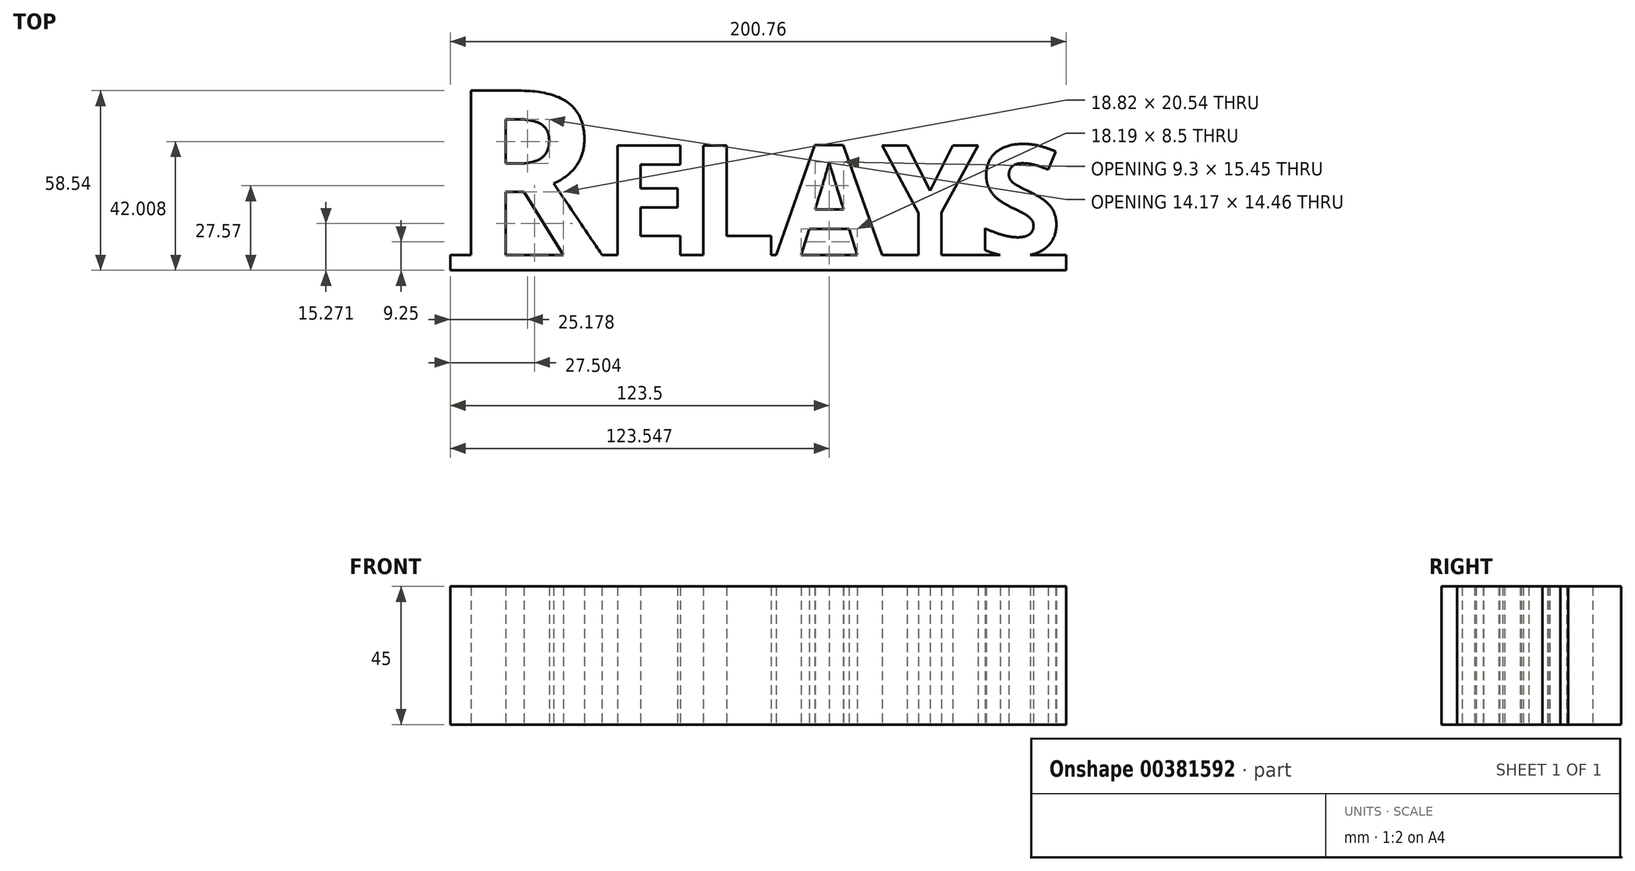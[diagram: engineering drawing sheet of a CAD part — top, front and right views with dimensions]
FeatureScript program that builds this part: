
annotation { "Feature Type Name" : "Feature", "Feature Type Description" : "" }
export const myFeature = defineFeature(function(context is Context, id is Id, definition is map)
    precondition{}
    {
        {
            var Q0;
            Q0=qCreatedBy(makeId("Top.planeOp"),FACE);
            var sketch = newSketch(context, id + "F0", { "sketchPlane" : qUnion([Q0])});
            skText(sketch, "E0", { "text": "ELAYS", "fontName": "OpenSans-Bold.ttf"});
            skText(sketch, "E1", { "text": "R", "fontName": "OpenSans-Bold.ttf"});
            skLineSegment(sketch, "E2", {"start": v(-50, 0) * mm, "end": v(150.76, 0) * mm});
            skLineSegment(sketch, "E3", {"start": v(150.76, -5) * mm, "end": v(-50, -5) * mm});
            skLineSegment(sketch, "E4", {"start": v(-50, -5) * mm, "end": v(-50, 0) * mm});
            skLineSegment(sketch, "E5", {"start": v(150.76, -5) * mm, "end": v(150.76, 0) * mm});
            const initialGuessF0  = {"E0": [0, 0, 1, 0, 0.036], "E1": [-0.05, 0, 1, 0, 0.054]};
            skSetInitialGuess(sketch, initialGuessF0);
            skSolve(sketch);
        }
        {
            var Q0;
            Q0=makeQuery(id+"F0.imprint","IMPRINT",FACE,{"disambiguationData":[TD([[makeQuery(id+"F0.imprint","IMPRINT",EDGE,{"derivedFrom":sQuery(id+"F0.wireOp",EDGE,"E3")}),-1.0]])]});
            extrude(context, id + "F1", {"entities" : qUnion([Q0]), "depth" : 45 * mm, "offsetDistance" : 25 * mm});
        }
        {
            var Q0;
            Q0=makeQuery(id+"F0.imprint","IMPRINT",FACE,{"disambiguationData":[TD([[makeQuery(id+"F0.imprint","IMPRINT",EDGE,{"derivedFrom":sQuery(id+"F0.wireOp",EDGE,"E1.sketch_text.stroke-0")}),-1.0]])]});
            var Q1;
            {var subQ0=sQuery(id+"F0.wireOp",EDGE,"E0.sketch_text.stroke-1");Q1=makeQuery(id+"F0.imprint","IMPRINT",FACE,{"disambiguationData":[TD([[makeQuery(id+"F0.imprint","IMPRINT",EDGE,{"derivedFrom":subQ0}),-1.0]])]});}
            var Q2;
            {var subQ0=sQuery(id+"F0.wireOp",EDGE,"E0.sketch_text.stroke-12");Q2=makeQuery(id+"F0.imprint","IMPRINT",FACE,{"disambiguationData":[TD([[makeQuery(id+"F0.imprint","IMPRINT",EDGE,{"derivedFrom":subQ0}),-1.0]])]});}
            var Q3;
            {var subQ1=sQuery(id+"F0.wireOp",EDGE,"E0.sketch_text.stroke-18");Q3=makeQuery(id+"F0.imprint","IMPRINT",FACE,{"disambiguationData":[TD([[makeQuery(id+"F0.imprint","IMPRINT",EDGE,{"derivedFrom":subQ1}),-1.0]])]});}
            var Q4;
            Q4=makeQuery(id+"F0.imprint","IMPRINT",FACE,{"disambiguationData":[TD([[makeQuery(id+"F0.imprint","IMPRINT",EDGE,{"derivedFrom":sQuery(id+"F0.wireOp",EDGE,"E0.sketch_text.stroke-30")}),-1.0]])]});
            extrude(context, id + "F2", {"entities" : qUnion([Q0, Q1, Q2, Q3, Q4]), "operationType" : NewBodyOperationType.ADD, "depth" : 45 * mm, "offsetDistance" : 25 * mm});
        }
        {
            var Q0;
            {var subQ6=sQuery(id+"F0.wireOp",EDGE,"E0.sketch_text.stroke-39");Q0=makeQuery(id+"F0.imprint","IMPRINT",FACE,{"disambiguationData":[TD([[makeQuery(id+"F0.imprint","IMPRINT",EDGE,{"derivedFrom":subQ6}),-1.0]])]});}
            var Q1;
            {var subQ0=sQuery(id+"F0.wireOp",EDGE,"E0.sketch_text.stroke-41");var subQ1=sQuery(id+"F0.wireOp",EDGE,"E0.sketch_text.stroke-40");var subQ2=makeQuery(id+"F0.imprint","INTERSECT",VERTEX,{"derivedFrom":[subQ1,subQ0]});Q1=makeQuery(id+"F0.imprint","IMPRINT",FACE,{"disambiguationData":[TD([[makeQuery(id+"F0.imprint","IMPRINT",EDGE,{"disambiguationData":[TD([[subQ2,1.0]])],"derivedFrom":subQ1}),-1.0]])]});}
            extrude(context, id + "F3", {"entities" : qUnion([Q0, Q1]), "operationType" : NewBodyOperationType.ADD, "depth" : 45 * mm, "offsetDistance" : 25 * mm});
        }
    });
